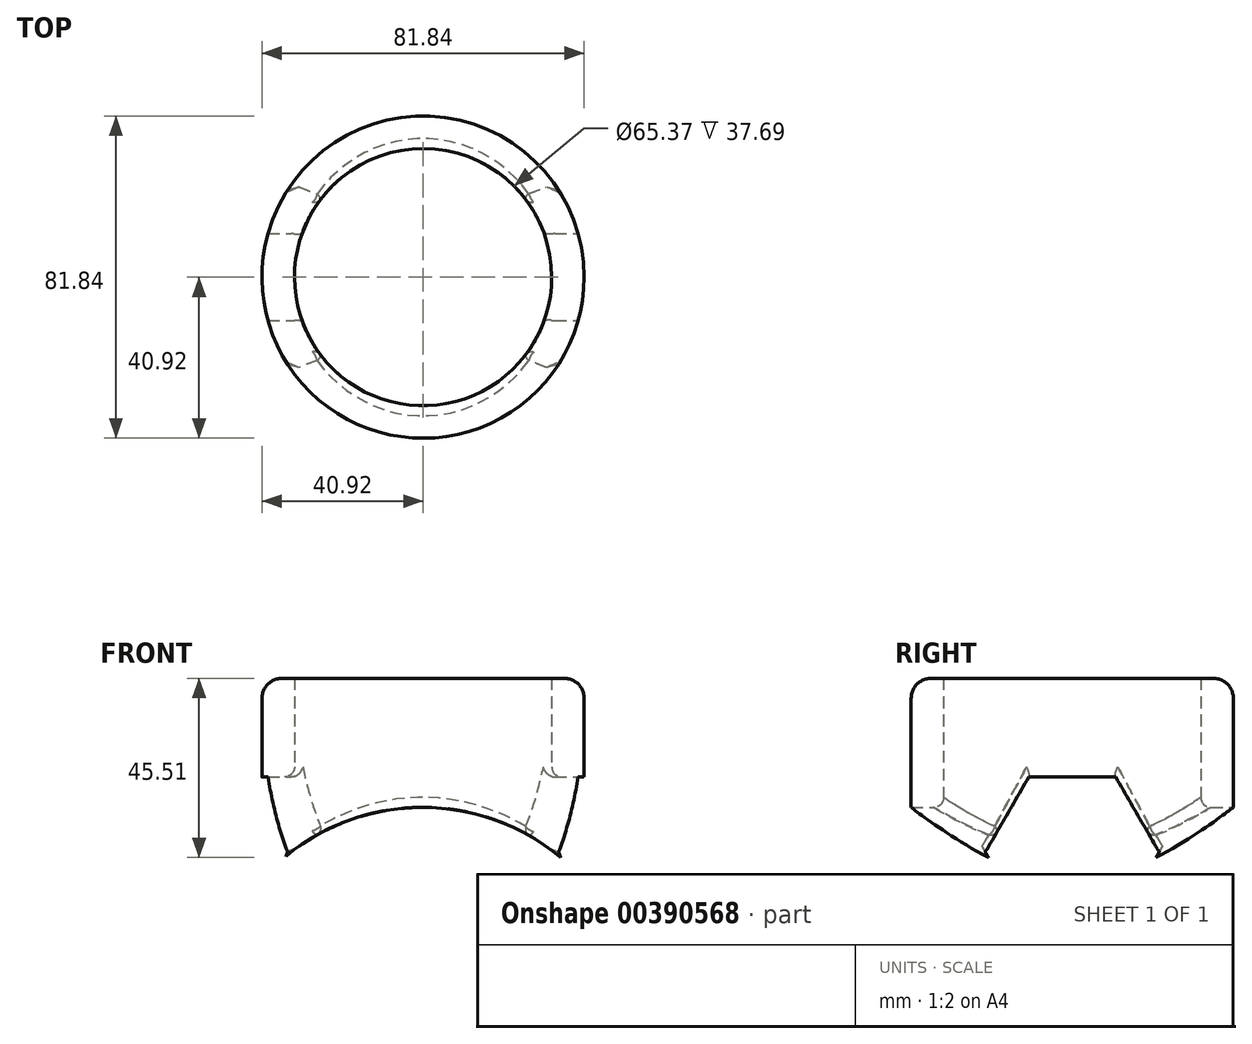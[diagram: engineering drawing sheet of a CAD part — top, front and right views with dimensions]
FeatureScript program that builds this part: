
annotation { "Feature Type Name" : "Feature", "Feature Type Description" : "" }
export const myFeature = defineFeature(function(context is Context, id is Id, definition is map)
    precondition{}
    {
        {
            var Q0;
            Q0=qCreatedBy(makeId("Top.planeOp"),FACE);
            var sketch = newSketch(context, id + "F0", { "sketchPlane" : qUnion([Q0])});
            skCircle(sketch, "E0", {"center": v(0, 0) * mm, "radius": 40.92 * mm});
            skCircle(sketch, "E1", {"center": v(0, 0) * mm, "radius": 32.68 * mm});
            skSolve(sketch);
        }
        {
            var Q0;
            Q0=makeQuery(id+"F0.imprint","IMPRINT",FACE,{"disambiguationData":[TD([[makeQuery(id+"F0.imprint","IMPRINT",EDGE,{"derivedFrom":sQuery(id+"F0.wireOp",EDGE,"E0")}),1.0]])]});
            extrude(context, id + "F1", {"entities" : qUnion([Q0]), "endBound" : BoundingType.SYMMETRIC, "depth" : 88.33 * mm});
        }
        {
            var Q0;
            Q0=qCreatedBy(makeId("Front.planeOp"),FACE);
            var sketch = newSketch(context, id + "F2", { "sketchPlane" : qUnion([Q0])});
            skCircle(sketch, "E2", {"center": v(-0.14, -43.43) * mm, "radius": 54.79 * mm});
            skSolve(sketch);
        }
        {
            var Q0;
            Q0=makeQuery(id+"F2.imprint","IMPRINT",FACE,{"disambiguationData":[TD([[makeQuery(id+"F2.imprint","IMPRINT",EDGE,{"derivedFrom":sQuery(id+"F2.wireOp",EDGE,"E2")}),1.0]])]});
            extrude(context, id + "F3", {"entities" : qUnion([Q0]), "operationType" : NewBodyOperationType.REMOVE, "endBound" : BoundingType.SYMMETRIC, "depth" : 126.84 * mm});
        }
        {
            var Q0;
            Q0=makeQuery(id+"F1.opExtrude","CAP_EDGE",EDGE,{"disambiguationData":[OSD([sQuery(id+"F0.wireOp",EDGE,"E0")])],"isStart":false});
            fillet(context, id + "F4", {"entities" : qUnion([Q0]), "radius" : 5.08 * mm, "tangentPropagation" : true, "allowEdgeOverflow" : false});
        }
        {
            var Q0;
            Q0=makeQuery(id+"F3.boolean.opBoolean","INTERSECT",EDGE,{"derivedFrom":[makeQuery(id+"F1.opExtrude","SWEPT_FACE",FACE,{"disambiguationData":[OSD([sQuery(id+"F0.wireOp",EDGE,"E1")])]}),makeQuery(id+"F3.opExtrude","SWEPT_FACE",FACE,{"disambiguationData":[OSD([sQuery(id+"F2.wireOp",EDGE,"E2")])]})]});
            fillet(context, id + "F5", {"entities" : qUnion([Q0]), "radius" : 2.54 * mm, "tangentPropagation" : true, "allowEdgeOverflow" : false});
        }
        {
            var Q0;
            Q0=qCreatedBy(makeId("Right.planeOp"),FACE);
            var sketch = newSketch(context, id + "F6", { "sketchPlane" : qUnion([Q0])});
            skCircle(sketch, "E3.cCircle", {"center": v(0, 0) * mm, "radius": 22.06 * mm, "construction": true});
            skLineSegment(sketch, "E3.0", {"start": v(22.06, 0) * mm, "end": v(11.03, -19.1) * mm});
            skLineSegment(sketch, "E3.1", {"start": v(11.03, -19.1) * mm, "end": v(-11.03, -19.1) * mm});
            skLineSegment(sketch, "E3.2", {"start": v(-11.03, -19.1) * mm, "end": v(-22.06, 0) * mm});
            skLineSegment(sketch, "E3.3", {"start": v(-22.06, 0) * mm, "end": v(-11.03, 19.1) * mm});
            skLineSegment(sketch, "E3.4", {"start": v(-11.03, 19.1) * mm, "end": v(11.03, 19.1) * mm});
            skLineSegment(sketch, "E3.5", {"start": v(11.03, 19.1) * mm, "end": v(22.06, 0) * mm});
            skSolve(sketch);
        }
        {
            var Q0;
            Q0=makeQuery(id+"F6.imprint","IMPRINT",FACE,{"disambiguationData":[TD([[makeQuery(id+"F6.imprint","IMPRINT",EDGE,{"derivedFrom":sQuery(id+"F6.wireOp",EDGE,"E3.0")}),-1.0]])]});
            extrude(context, id + "F7", {"entities" : qUnion([Q0]), "operationType" : NewBodyOperationType.REMOVE, "endBound" : BoundingType.SYMMETRIC, "oppositeDirection" : true, "depth" : 143.36 * mm});
        }
        {
            var Q0;
            Q0=makeQuery(id+"F7.boolean.opBoolean","INTERSECT",EDGE,{"disambiguationData":[OD(1.0)],"derivedFrom":[makeQuery(id+"F1.opExtrude","SWEPT_FACE",FACE,{"disambiguationData":[OSD([sQuery(id+"F0.wireOp",EDGE,"E1")])]}),makeQuery(id+"F7.opExtrude","SWEPT_FACE",FACE,{"disambiguationData":[OSD([sQuery(id+"F6.wireOp",EDGE,"E3.5")])]})]});
            var Q1;
            Q1=makeQuery(id+"F7.boolean.opBoolean","INTERSECT",EDGE,{"disambiguationData":[OD(0.0)],"derivedFrom":[makeQuery(id+"F1.opExtrude","SWEPT_FACE",FACE,{"disambiguationData":[OSD([sQuery(id+"F0.wireOp",EDGE,"E1")])]}),makeQuery(id+"F7.opExtrude","SWEPT_FACE",FACE,{"disambiguationData":[OSD([sQuery(id+"F6.wireOp",EDGE,"E3.3")])]})]});
            var Q2;
            Q2=makeQuery(id+"F7.boolean.opBoolean","INTERSECT",EDGE,{"disambiguationData":[OD(0.0)],"derivedFrom":[makeQuery(id+"F1.opExtrude","SWEPT_FACE",FACE,{"disambiguationData":[OSD([sQuery(id+"F0.wireOp",EDGE,"E1")])]}),makeQuery(id+"F7.opExtrude","SWEPT_FACE",FACE,{"disambiguationData":[OSD([sQuery(id+"F6.wireOp",EDGE,"E3.4")])]})]});
            var Q3;
            Q3=makeQuery(id+"F7.boolean.opBoolean","INTERSECT",EDGE,{"disambiguationData":[OD(0.0)],"derivedFrom":[makeQuery(id+"F1.opExtrude","SWEPT_FACE",FACE,{"disambiguationData":[OSD([sQuery(id+"F0.wireOp",EDGE,"E1")])]}),makeQuery(id+"F7.opExtrude","SWEPT_FACE",FACE,{"disambiguationData":[OSD([sQuery(id+"F6.wireOp",EDGE,"E3.5")])]})]});
            var Q4;
            Q4=makeQuery(id+"F7.boolean.opBoolean","INTERSECT",EDGE,{"disambiguationData":[OD(1.0)],"derivedFrom":[makeQuery(id+"F1.opExtrude","SWEPT_FACE",FACE,{"disambiguationData":[OSD([sQuery(id+"F0.wireOp",EDGE,"E1")])]}),makeQuery(id+"F7.opExtrude","SWEPT_FACE",FACE,{"disambiguationData":[OSD([sQuery(id+"F6.wireOp",EDGE,"E3.3")])]})]});
            var Q5;
            Q5=makeQuery(id+"F7.boolean.opBoolean","INTERSECT",EDGE,{"disambiguationData":[OD(1.0)],"derivedFrom":[makeQuery(id+"F1.opExtrude","SWEPT_FACE",FACE,{"disambiguationData":[OSD([sQuery(id+"F0.wireOp",EDGE,"E1")])]}),makeQuery(id+"F7.opExtrude","SWEPT_FACE",FACE,{"disambiguationData":[OSD([sQuery(id+"F6.wireOp",EDGE,"E3.4")])]})]});
            fillet(context, id + "F8", {"entities" : qUnion([Q0, Q1, Q2, Q3, Q4, Q5]), "radius" : 2.54 * mm, "tangentPropagation" : true, "allowEdgeOverflow" : false});
        }
    });
